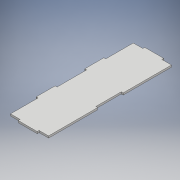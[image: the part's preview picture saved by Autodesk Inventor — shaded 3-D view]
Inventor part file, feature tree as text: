
AUTODESK INVENTOR PART (.ipt)
format: ipt  version: 2017 (Build 210142000, 142)  size: 138,752 bytes
history: native  units: mm
features: extrude x1, sketch x1
ambient origin geometry x8: Origin, YZ Plane, XZ Plane, XY Plane, X Axis, Y Axis, Z Axis, Center Point
bodies: Solid1 (feature_tree)
feature tree (2):
  extrude  "Extrusion1"  [1 undecoded]
  sketch  "Sketch1"  dims[d26=3.0mm d27=0.0mm d47=193.0mm d48=60.0mm d49=3.0mm d50=30.0mm d51=15.0mm d52=3.0mm d53=3.0mm d54=15.0mm d55=3.0mm d56=3.0mm d57=3.0mm d58=3.0mm d59=15.0mm d60=40.0mm d61=3.0mm d62=77.0mm d63=3.0mm d64=76.0mm d65=199.145723mm d66=43.3mm d67=46.6mm d68=43.3mm d69=30.0mm d70=29.8mm]
note: 1 required parameter value undecoded (feature->parameter linkage not recoverable at this tier; creation-order binding heuristic only, values carry confidence <= 0.55)
